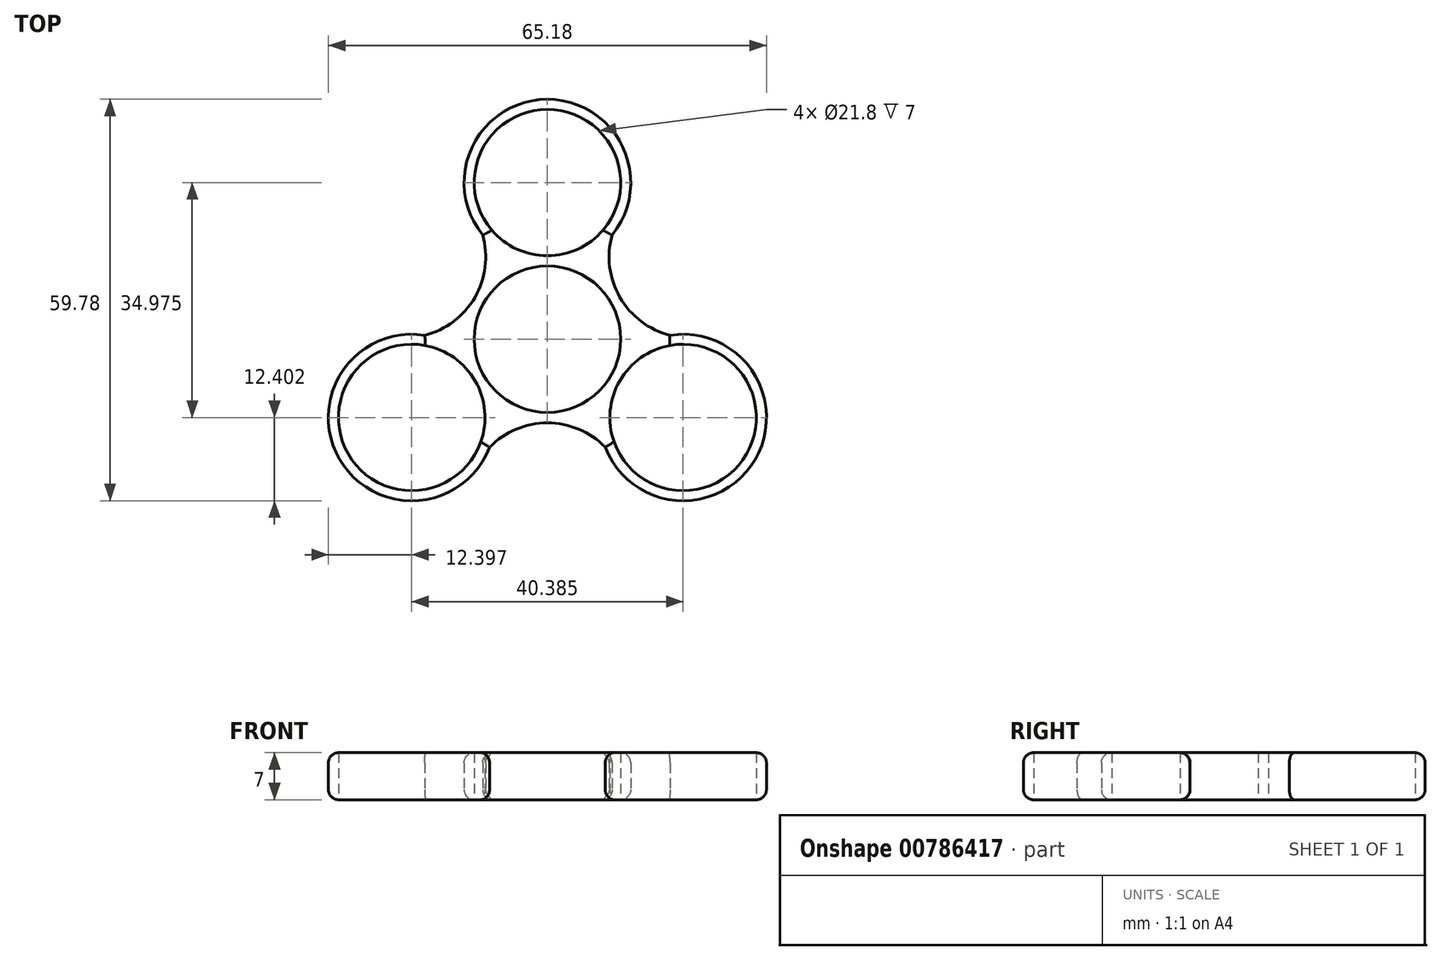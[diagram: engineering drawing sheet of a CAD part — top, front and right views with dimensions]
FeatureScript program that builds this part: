
annotation { "Feature Type Name" : "Feature", "Feature Type Description" : "" }
export const myFeature = defineFeature(function(context is Context, id is Id, definition is map)
    precondition{}
    {
        {
            var Q0;
            Q0=qCreatedBy(makeId("Top.planeOp"),FACE);
            var sketch = newSketch(context, id + "F0", { "sketchPlane" : qUnion([Q0])});
            skCircle(sketch, "E0", {"center": v(0, 0) * mm, "radius": 10.9 * mm});
            skArc(sketch, "E1", {"start": v(9.63, 15.5) * mm, "mid": v(0, 35.72) * mm, "end": v(-9.63, 15.5) * mm});
            skCircle(sketch, "E2", {"center": v(0, 23.32) * mm, "radius": 10.9 * mm});
            skArc(sketch, "E3.1.0", {"start": v(-18.24, 0.59) * mm, "mid": v(-30.93, -17.86) * mm, "end": v(-8.61, -16.09) * mm});
            skCircle(sketch, "E3.1.1", {"center": v(-20.2, -11.66) * mm, "radius": 10.9 * mm});
            skArc(sketch, "E3.2.0", {"start": v(8.61, -16.09) * mm, "mid": v(30.93, -17.86) * mm, "end": v(18.24, 0.59) * mm});
            skCircle(sketch, "E3.2.1", {"center": v(20.2, -11.66) * mm, "radius": 10.9 * mm});
            skArc(sketch, "E4", {"start": v(-18.24, 0.59) * mm, "mid": v(-10.79, 6.23) * mm, "end": v(-9.63, 15.5) * mm});
            skArc(sketch, "E5.1.0", {"start": v(8.61, -16.09) * mm, "mid": v(0, -12.46) * mm, "end": v(-8.61, -16.09) * mm});
            skArc(sketch, "E5.2.0", {"start": v(9.63, 15.5) * mm, "mid": v(10.79, 6.23) * mm, "end": v(18.24, 0.59) * mm});
            skPoint(sketch, "E6.orphan", {"position": v(-11.92, 19.89) * mm});
            skPoint(sketch, "E7.orphan", {"position": v(11.92, 19.89) * mm});
            skPoint(sketch, "E8.orphan", {"position": v(-23.18, 0.38) * mm});
            skPoint(sketch, "E9.orphan", {"position": v(-11.26, -20.26) * mm});
            skPoint(sketch, "E10.orphan", {"position": v(11.26, -20.26) * mm});
            skPoint(sketch, "E11.orphan", {"position": v(23.18, 0.38) * mm});
            skSolve(sketch);
        }
        {
            var Q0;
            Q0=makeQuery(id+"F0.imprint","IMPRINT",FACE,{"disambiguationData":[TD([[makeQuery(id+"F0.imprint","IMPRINT",EDGE,{"derivedFrom":sQuery(id+"F0.wireOp",EDGE,"E0")}),-1.0]])]});
            extrude(context, id + "F1", {"entities" : qUnion([Q0]), "depth" : 7 * mm, "offsetDistance" : 25 * mm});
        }
        {
            var Q0;
            Q0=makeQuery(id+"F1.opExtrude","CAP_EDGE",EDGE,{"disambiguationData":[OSD([sQuery(id+"F0.wireOp",EDGE,"E4")])],"isStart":false});
            var Q1;
            Q1=makeQuery(id+"F1.opExtrude","CAP_EDGE",EDGE,{"disambiguationData":[OSD([sQuery(id+"F0.wireOp",EDGE,"E5.2.0")])],"isStart":false});
            var Q2;
            Q2=makeQuery(id+"F1.opExtrude","CAP_EDGE",EDGE,{"disambiguationData":[OSD([sQuery(id+"F0.wireOp",EDGE,"E5.1.0")])],"isStart":false});
            var Q3;
            Q3=makeQuery(id+"F1.opExtrude","CAP_EDGE",EDGE,{"disambiguationData":[OSD([sQuery(id+"F0.wireOp",EDGE,"E1")])],"isStart":false});
            var Q4;
            Q4=makeQuery(id+"F1.opExtrude","CAP_EDGE",EDGE,{"disambiguationData":[OSD([sQuery(id+"F0.wireOp",EDGE,"E3.2.0")])],"isStart":false});
            var Q5;
            Q5=makeQuery(id+"F1.opExtrude","CAP_EDGE",EDGE,{"disambiguationData":[OSD([sQuery(id+"F0.wireOp",EDGE,"E3.1.0")])],"isStart":false});
            var Q6;
            Q6=makeQuery(id+"F1.opExtrude","CAP_EDGE",EDGE,{"disambiguationData":[OSD([sQuery(id+"F0.wireOp",EDGE,"E5.2.0")])],"isStart":true});
            var Q7;
            Q7=makeQuery(id+"F1.opExtrude","CAP_EDGE",EDGE,{"disambiguationData":[OSD([sQuery(id+"F0.wireOp",EDGE,"E3.2.0")])],"isStart":true});
            var Q8;
            Q8=makeQuery(id+"F1.opExtrude","CAP_EDGE",EDGE,{"disambiguationData":[OSD([sQuery(id+"F0.wireOp",EDGE,"E5.1.0")])],"isStart":true});
            var Q9;
            Q9=makeQuery(id+"F1.opExtrude","CAP_EDGE",EDGE,{"disambiguationData":[OSD([sQuery(id+"F0.wireOp",EDGE,"E4")])],"isStart":true});
            var Q10;
            Q10=makeQuery(id+"F1.opExtrude","CAP_EDGE",EDGE,{"disambiguationData":[OSD([sQuery(id+"F0.wireOp",EDGE,"E1")])],"isStart":true});
            var Q11;
            Q11=makeQuery(id+"F1.opExtrude","CAP_EDGE",EDGE,{"disambiguationData":[OSD([sQuery(id+"F0.wireOp",EDGE,"E3.1.0")])],"isStart":true});
            fillet(context, id + "F2", {"entities" : qUnion([Q0, Q1, Q2, Q3, Q4, Q5, Q6, Q7, Q8, Q9, Q10, Q11]), "radius" : 1.5 * mm, "tangentPropagation" : true, "allowEdgeOverflow" : false});
        }
    });
